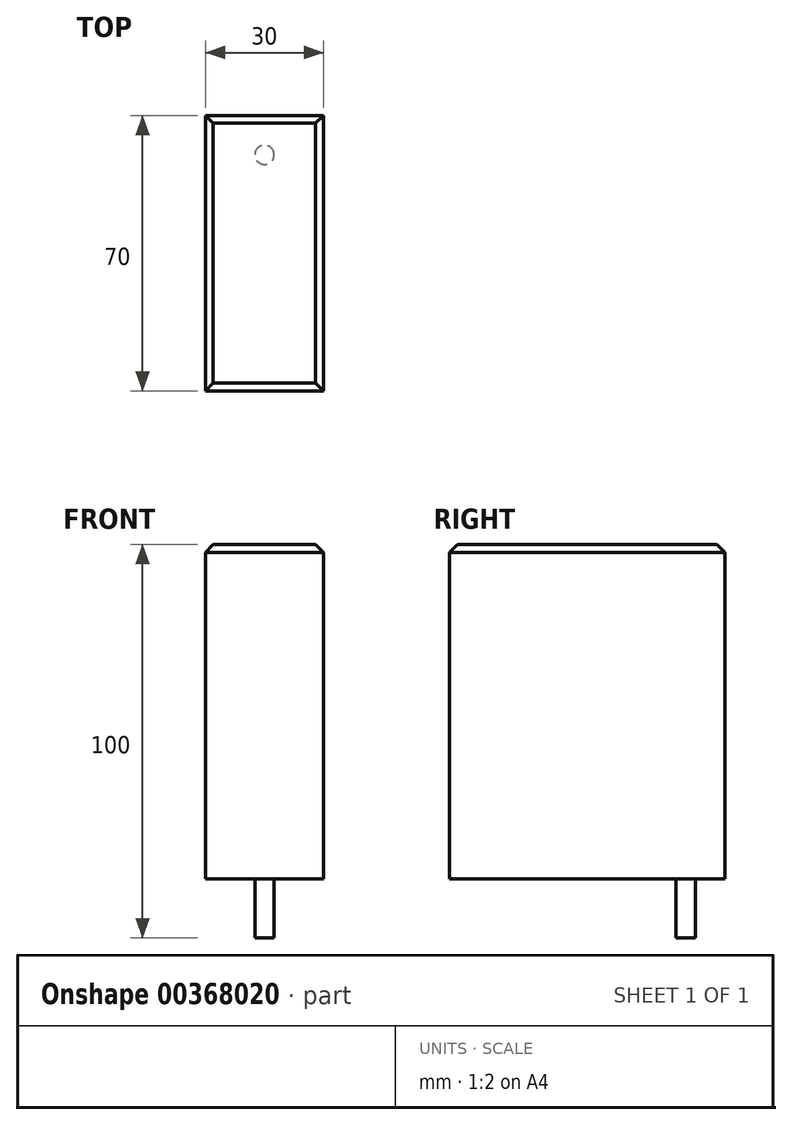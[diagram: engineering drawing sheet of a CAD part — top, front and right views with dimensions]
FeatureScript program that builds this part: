
annotation { "Feature Type Name" : "Feature", "Feature Type Description" : "" }
export const myFeature = defineFeature(function(context is Context, id is Id, definition is map)
    precondition{}
    {
        {
            var Q0;
            Q0=qCreatedBy(makeId("Front.planeOp"),FACE);
            var sketch = newSketch(context, id + "F0", { "sketchPlane" : qUnion([Q0])});
            skLineSegment(sketch, "E0.top", {"start": v(-10.2, -46.23) * mm, "end": v(19.8, -46.23) * mm});
            skLineSegment(sketch, "E0.left", {"start": v(-10.2, 53.77) * mm, "end": v(-10.2, -46.23) * mm});
            skLineSegment(sketch, "E0.right", {"start": v(19.8, 53.77) * mm, "end": v(19.8, -46.23) * mm});
            skLineSegment(sketch, "E1", {"start": v(4.8, 70.03) * mm, "end": v(4.8, -46.23) * mm, "construction": true});
            skPoint(sketch, "E1.startSnap0", {"position": v(4.8, 53.77) * mm});
            skPoint(sketch, "E2.orphan", {"position": v(58.59, 101.57) * mm});
            skPoint(sketch, "E3.orphan", {"position": v(-49, 101.57) * mm});
            skLineSegment(sketch, "E4", {"start": v(-10.2, 53.77) * mm, "end": v(19.8, 53.77) * mm});
            skSolve(sketch);
        }
        {
            var Q0;
            Q0=makeQuery(id+"F0.imprint","IMPRINT",FACE,{"disambiguationData":[TD([[makeQuery(id+"F0.imprint","IMPRINT",EDGE,{"derivedFrom":sQuery(id+"F0.wireOp",EDGE,"E0.top")}),1.0]])]});
            extrude(context, id + "F1", {"entities" : qUnion([Q0]), "depth" : 70 * mm});
        }
        {
            var Q0;
            Q0=makeQuery(id+"F1.opExtrude","SWEPT_FACE",FACE,{"disambiguationData":[OSD([sQuery(id+"F0.wireOp",EDGE,"E0.top")])]});
            var sketch = newSketch(context, id + "F2", { "sketchPlane" : qUnion([Q0])});
            skLineSegment(sketch, "E5", {"start": v(4.8, 70) * mm, "end": v(4.8, 22.68) * mm, "construction": true});
            skPoint(sketch, "E5.endSnap0", {"position": v(4.8, 70) * mm});
            skCircle(sketch, "E6", {"center": v(4.8, 60) * mm, "radius": 2.45 * mm});
            skLineSegment(sketch, "E7", {"start": v(19.8, 35) * mm, "end": v(-15.94, 35) * mm, "construction": true});
            skPoint(sketch, "E7.endSnap0", {"position": v(-10.2, 35) * mm});
            skCircle(sketch, "E8.MirrorC", {"center": v(4.8, 10) * mm, "radius": 2.45 * mm});
            skSolve(sketch);
        }
        {
            var Q0;
            Q0=makeQuery(id+"F2.imprint","IMPRINT",FACE,{"disambiguationData":[TD([[makeQuery(id+"F2.imprint","IMPRINT",EDGE,{"derivedFrom":sQuery(id+"F2.wireOp",EDGE,"E6")}),1.0]])]});
            var Q1;
            Q1=makeQuery(id+"F2.imprint","IMPRINT",FACE,{"disambiguationData":[TD([[makeQuery(id+"F2.imprint","IMPRINT",EDGE,{"derivedFrom":sQuery(id+"F2.wireOp",EDGE,"E8.MirrorC")}),-1.0]])]});
            extrude(context, id + "F3", {"entities" : qUnion([Q0, Q1]), "operationType" : NewBodyOperationType.REMOVE, "oppositeDirection" : true, "depth" : 15 * mm});
        }
        {
            var Q0;
            Q0=makeQuery(id+"F1.opExtrude","CAP_EDGE",EDGE,{"disambiguationData":[OSD([sQuery(id+"F0.wireOp",EDGE,"E4")])],"isStart":false});
            var Q1;
            Q1=makeQuery(id+"F1.opExtrude","SWEPT_EDGE",EDGE,{"disambiguationData":[OSD([sQuery(id+"F0.wireOp",EDGE,"E0.right"),sQuery(id+"F0.wireOp",EDGE,"E4")])]});
            var Q2;
            Q2=makeQuery(id+"F1.opExtrude","CAP_EDGE",EDGE,{"disambiguationData":[OSD([sQuery(id+"F0.wireOp",EDGE,"E4")])],"isStart":true});
            var Q3;
            Q3=makeQuery(id+"F1.opExtrude","SWEPT_EDGE",EDGE,{"disambiguationData":[OSD([sQuery(id+"F0.wireOp",EDGE,"E0.left"),sQuery(id+"F0.wireOp",EDGE,"E4")])]});
            chamfer(context, id + "F4", {"entities" : qUnion([Q0, Q1, Q2, Q3]), "width" : 2 * mm, "tangentPropagation" : true});
        }
    });
